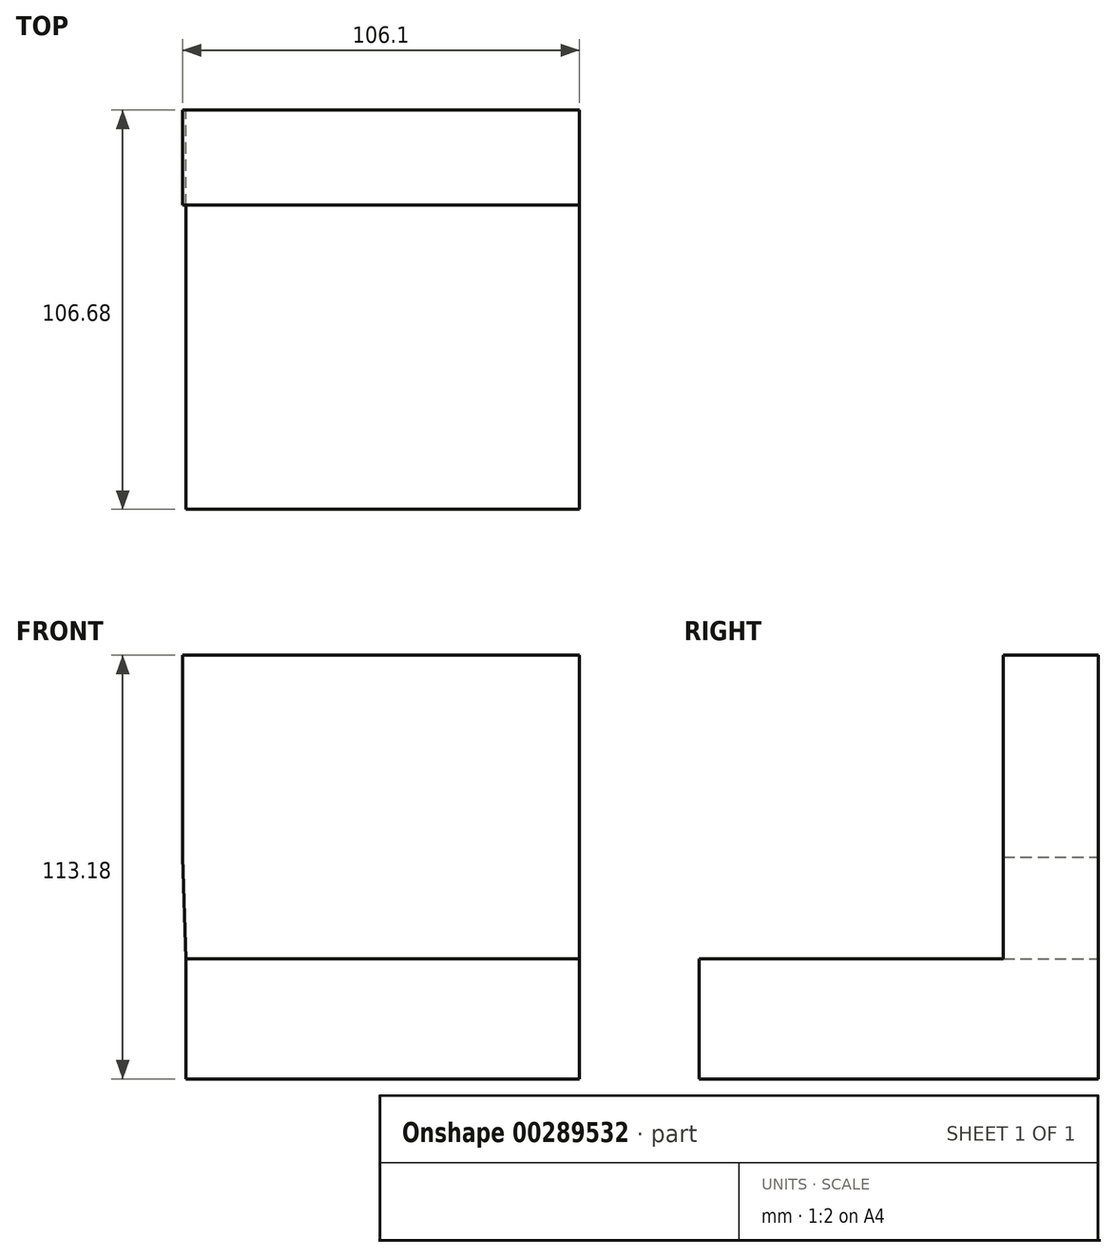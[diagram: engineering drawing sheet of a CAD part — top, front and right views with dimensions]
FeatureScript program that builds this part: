
annotation { "Feature Type Name" : "Feature", "Feature Type Description" : "" }
export const myFeature = defineFeature(function(context is Context, id is Id, definition is map)
    precondition{}
    {
        {
            var Q0;
            Q0=qCreatedBy(makeId("Front.planeOp"),FACE);
            var sketch = newSketch(context, id + "F0", { "sketchPlane" : qUnion([Q0])});
            skLineSegment(sketch, "E0.bottom", {"start": v(-57.42, 64.55) * mm, "end": v(48.68, 64.55) * mm});
            skLineSegment(sketch, "E0.top", {"start": v(-57.42, 10.63) * mm, "end": v(48.68, 10.63) * mm});
            skLineSegment(sketch, "E0.left", {"start": v(-57.42, 64.55) * mm, "end": v(-57.42, 10.63) * mm});
            skLineSegment(sketch, "E0.right", {"start": v(48.68, 64.55) * mm, "end": v(48.68, 10.63) * mm});
            skLineSegment(sketch, "E1.bottom", {"start": v(-56.55, -16.57) * mm, "end": v(48.68, -16.57) * mm});
            skLineSegment(sketch, "E1.top", {"start": v(-56.55, -48.63) * mm, "end": v(48.68, -48.63) * mm});
            skLineSegment(sketch, "E1.left", {"start": v(-56.55, -16.57) * mm, "end": v(-56.55, -48.63) * mm});
            skLineSegment(sketch, "E1.right", {"start": v(48.68, -16.57) * mm, "end": v(48.68, -48.63) * mm});
            skLineSegment(sketch, "E2", {"start": v(-57.42, 10.63) * mm, "end": v(-56.55, -16.57) * mm});
            skLineSegment(sketch, "E3", {"start": v(48.68, 10.63) * mm, "end": v(48.68, -16.57) * mm});
            skSolve(sketch);
        }
        {
            var Q0;
            Q0=makeQuery(id+"F0.imprint","IMPRINT",FACE,{"disambiguationData":[TD([[makeQuery(id+"F0.imprint","IMPRINT",EDGE,{"derivedFrom":sQuery(id+"F0.wireOp",EDGE,"E1.bottom")}),-1.0]])]});
            extrude(context, id + "F1", {"entities" : qUnion([Q0]), "depth" : 106.68 * mm});
        }
        {
            var Q0;
            Q0 = qSketchRegion(id + "F0", true);
            extrude(context, id + "F2", {"entities" : qUnion([Q0]), "operationType" : NewBodyOperationType.ADD, "depth" : 25.4 * mm});
        }
        {
            var Q0;
            Q0 = qSketchRegion(id + "F0", true);
            extrude(context, id + "F3", {"entities" : qUnion([Q0]), "operationType" : NewBodyOperationType.ADD, "depth" : 25.4 * mm});
        }
    });
